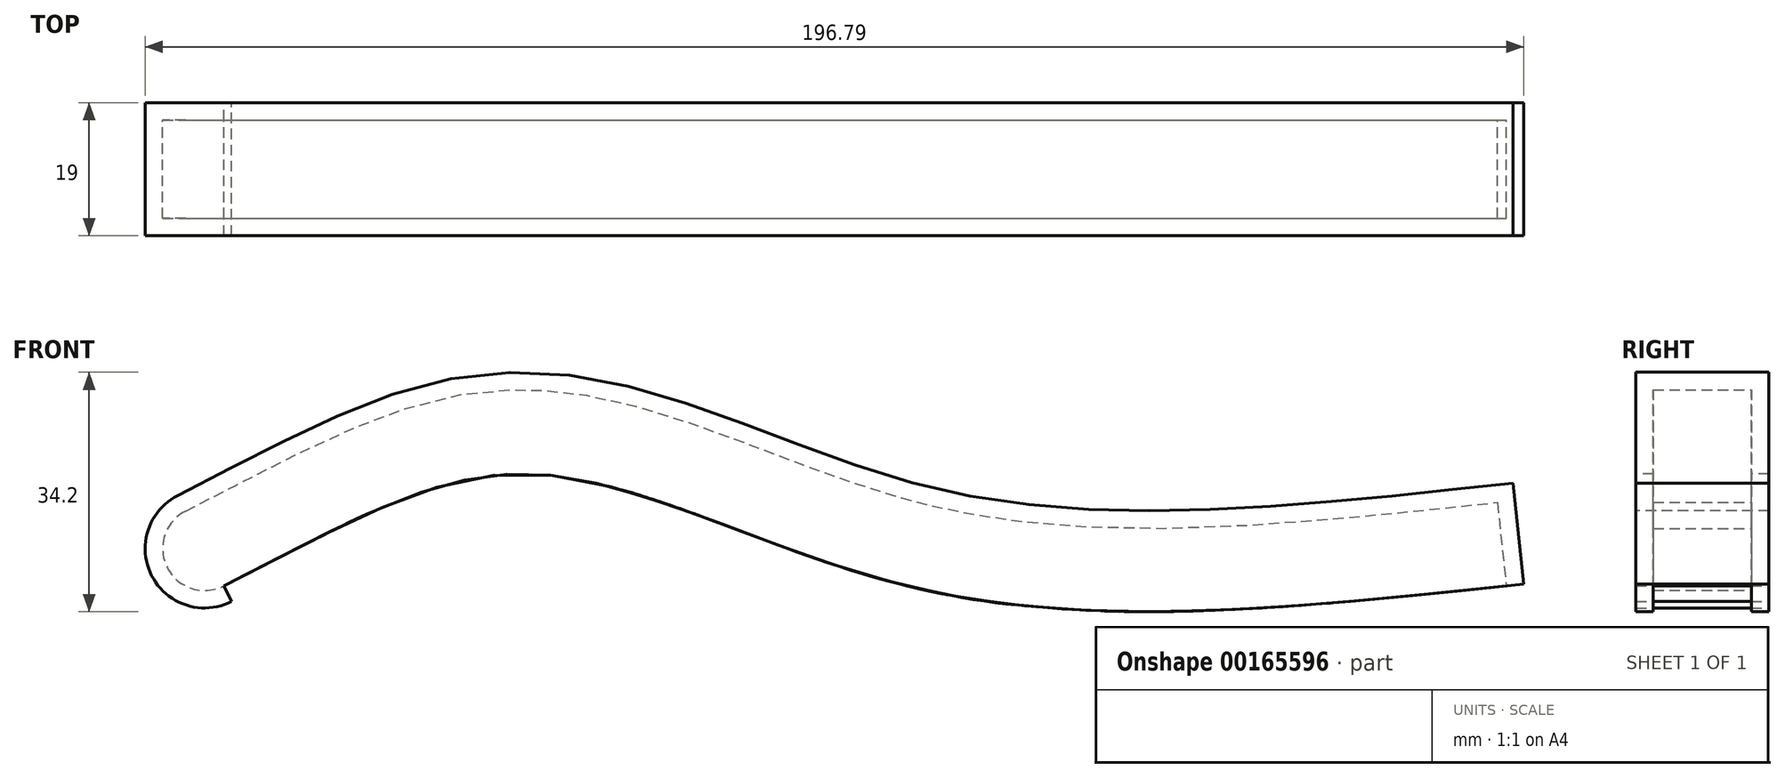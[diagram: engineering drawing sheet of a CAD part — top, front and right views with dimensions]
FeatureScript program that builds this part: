
annotation { "Feature Type Name" : "Feature", "Feature Type Description" : "" }
export const myFeature = defineFeature(function(context is Context, id is Id, definition is map)
    precondition{}
    {
        {
            var Q0;
            Q0=qCreatedBy(makeId("Front.planeOp"),FACE);
            var sketch = newSketch(context, id + "F0", { "sketchPlane" : qUnion([Q0])});
            skFitSpline(sketch, "E0", {"points": [v(0, 0) * mm, v(45.03, 15.95) * mm, v(97.44, 0) * mm, v(183.09, 0) * mm], "startDerivative": vector(194.9, 99.12) * mm, "endDerivative": vector(260.8, 27.81) * mm});
            skFitSpline(sketch, "E1.0", {"points": [v(-5.44, 10.7) * mm, v(-1.45, 12.72) * mm, v(4.13, 15.64) * mm, v(11.14, 19.16) * mm, v(16.28, 21.58) * mm, v(21.42, 23.74) * mm, v(26.65, 25.58) * mm, v(32.05, 27) * mm, v(36.73, 27.73) * mm, v(40.58, 28) * mm, v(43.02, 28.04) * mm, v(44.98, 27.98) * mm, v(46.97, 27.85) * mm, v(49.4, 27.6) * mm, v(52.3, 27.14) * mm, v(56.08, 26.37) * mm, v(60.72, 25.16) * mm, v(66.19, 23.42) * mm, v(71.59, 21.5) * mm, v(76.95, 19.48) * mm, v(82.28, 17.47) * mm, v(87.58, 15.53) * mm, v(91.97, 14.04) * mm, v(95.46, 12.96) * mm, v(97.63, 12.35) * mm, v(99.36, 11.89) * mm, v(101.09, 11.46) * mm, v(103.26, 10.96) * mm, v(105.9, 10.43) * mm, v(109.49, 9.81) * mm, v(114.07, 9.19) * mm, v(119.76, 8.68) * mm, v(127.63, 8.29) * mm, v(138.02, 8.3) * mm, v(151.47, 9.02) * mm, v(165.97, 10.27) * mm, v(176.4, 11.35) * mm, v(181.81, 11.93) * mm]});
            skArc(sketch, "E2", {"start": v(-5.44, 10.7) * mm, "mid": v(-8.07, 2.63) * mm, "end": v(0, 0) * mm});
            skLineSegment(sketch, "E3", {"start": v(181.81, 11.93) * mm, "end": v(183.09, 0) * mm});
            skSolve(sketch);
        }
        {
            var Q0;
            Q0 = qSketchRegion(id + "F0", true);
            extrude(context, id + "F1", {"entities" : qUnion([Q0]), "endBound" : BoundingType.SYMMETRIC, "depth" : 14 * mm});
        }
        {
            var Q0;
            Q0=makeQuery(id+"F1.opExtrude","SWEPT_FACE",FACE,{"disambiguationData":[OSD([sQuery(id+"F0.wireOp",EDGE,"E0")])]});
            shell(context, id + "F2", {"entities" : qUnion([Q0]), "thickness" : 2.5 * mm, "oppositeDirection" : true});
        }
    });
